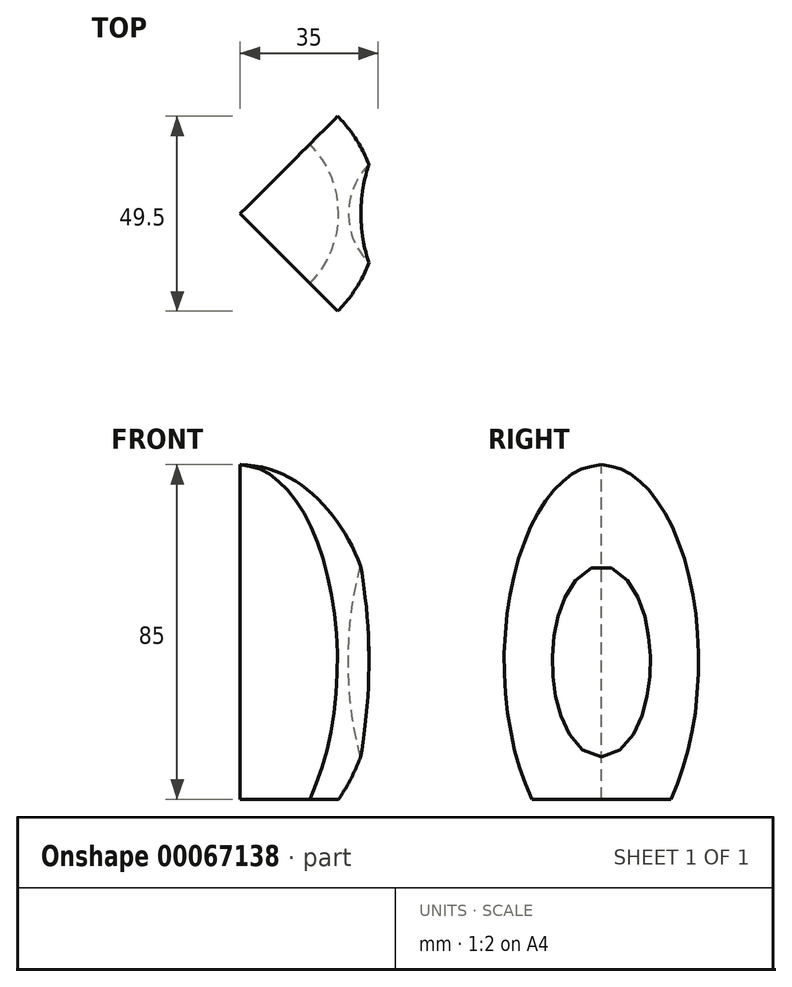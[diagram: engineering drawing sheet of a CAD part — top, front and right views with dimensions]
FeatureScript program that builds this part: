
annotation { "Feature Type Name" : "Feature", "Feature Type Description" : "" }
export const myFeature = defineFeature(function(context is Context, id is Id, definition is map)
    precondition{}
    {
        {
            var Q0;
            Q0=qCreatedBy(makeId("Front.planeOp"),FACE);
            var sketch = newSketch(context, id + "F0", { "sketchPlane" : qUnion([Q0])});
            skEllipticalArc(sketch, "E0", {});
            skLineSegment(sketch, "E1", {"start": v(0, 50) * mm, "end": v(0, -35) * mm, "construction": true});
            skLineSegment(sketch, "E2", {"start": v(0, 0) * mm, "end": v(35, 0) * mm, "construction": true});
            skLineSegment(sketch, "E3", {"start": v(0, -35) * mm, "end": v(25, -35) * mm});
            skLineSegment(sketch, "E4", {"start": v(0, 50) * mm, "end": v(0, -35) * mm});
            skPoint(sketch, "E5.orphan", {"position": v(-25, -35) * mm});
            skPoint(sketch, "E6.orphan", {"position": v(0, -50) * mm});
            const initialGuessF0  = {"E0": [0, 0, 0, 1, 0.05, 0.035, 3.936991483773937, 0]};
            skSetInitialGuess(sketch, initialGuessF0);
            skSolve(sketch);
        }
        {
            var Q0;
            Q0 = qSketchRegion(id + "F0", true);
            var Q1;
            Q1=sQuery(id+"F0.wireOp",EDGE,"E4");
            revolve(context, id + "F1", {"entities" : qUnion([Q0]), "axis" : qUnion([Q1]), "revolveType" : RevolveType.FULL});
        }
        {
            var Q0;
            Q0=qCreatedBy(makeId("Front.planeOp"),FACE);
            var sketch = newSketch(context, id + "F2", { "sketchPlane" : qUnion([Q0])});
            skEllipticalArc(sketch, "E7", {});
            skLineSegment(sketch, "E8", {"start": v(45, 42.5) * mm, "end": v(45, -42.5) * mm});
            const initialGuessF2  = {"E7": [0.045, 0, -1, 0, 0.0175, 0.0425, 4.71238898038469, 1.5707963267948966]};
            skSetInitialGuess(sketch, initialGuessF2);
            skSolve(sketch);
        }
        {
            var Q0;
            Q0 = qSketchRegion(id + "F2", true);
            var Q1;
            Q1=sQuery(id+"F2.wireOp",EDGE,"E8");
            revolve(context, id + "F3", {"operationType" : NewBodyOperationType.REMOVE, "entities" : qUnion([Q0]), "axis" : qUnion([Q1]), "revolveType" : RevolveType.FULL, "oppositeDirection" : true});
        }
        {
            var Q0;
            Q0=qCreatedBy(makeId("Top.planeOp"),FACE);
            var sketch = newSketch(context, id + "F4", { "sketchPlane" : qUnion([Q0])});
            skLineSegment(sketch, "E9", {"start": v(0, 0) * mm, "end": v(45, 45) * mm});
            skLineSegment(sketch, "E10", {"start": v(45, 45) * mm, "end": v(-45, 45) * mm});
            skLineSegment(sketch, "E11", {"start": v(-45, 45) * mm, "end": v(-45, -45) * mm});
            skLineSegment(sketch, "E12", {"start": v(-45, -45) * mm, "end": v(45, -45) * mm});
            skLineSegment(sketch, "E13", {"start": v(45, -45) * mm, "end": v(0, 0) * mm});
            skLineSegment(sketch, "E14", {"start": v(0, 0) * mm, "end": v(-45, 0) * mm, "construction": true});
            skSolve(sketch);
        }
        {
            var Q0;
            Q0 = qSketchRegion(id + "F4", true);
            extrude(context, id + "F5", {"entities" : qUnion([Q0]), "operationType" : NewBodyOperationType.REMOVE, "endBound" : BoundingType.THROUGH_ALL, "oppositeDirection" : true, "depth" : 25 * mm, "hasSecondDirection" : true, "secondDirectionBound" : SecondDirectionBoundingType.THROUGH_ALL, "secondDirectionOppositeDirection" : false, "secondDirectionDepth" : 25 * mm});
        }
        {
            var Q0;
            Q0=qCreatedBy(makeId("Front.planeOp"),FACE);
            var sketch = newSketch(context, id + "F6", { "sketchPlane" : qUnion([Q0])});
            skLineSegment(sketch, "E15", {"start": v(0, 47) * mm, "end": v(0, -32) * mm});
            skLineSegment(sketch, "E16", {"start": v(0, 47) * mm, "end": v(6, 47) * mm});
            skLineSegment(sketch, "E17", {"start": v(6, 47) * mm, "end": v(6, -17) * mm});
            skLineSegment(sketch, "E18", {"start": v(6, -17) * mm, "end": v(14, -17) * mm, "construction": true});
            skEllipticalArc(sketch, "E19", {});
            skLineSegment(sketch, "E20", {"start": v(14, -17) * mm, "end": v(14, -32) * mm, "construction": true});
            skLineSegment(sketch, "E21", {"start": v(14, -32) * mm, "end": v(0, -32) * mm});
            const initialGuessF6  = {"E19": [0.014, -0.017, -1, 0, 0.008, 0.015, 6.283185307179586, 1.5707963267948972]};
            skSetInitialGuess(sketch, initialGuessF6);
            skSolve(sketch);
        }
        {
            var Q0;
            Q0 = qSketchRegion(id + "F6", true);
            var Q1;
            Q1=sQuery(id+"F6.wireOp",EDGE,"E15");
            revolve(context, id + "F7", {"operationType" : NewBodyOperationType.ADD, "entities" : qUnion([Q0]), "axis" : qUnion([Q1]), "revolveType" : RevolveType.ONE_DIRECTION, "oppositeDirection" : true, "angle" : 45 * degree});
        }
    });
